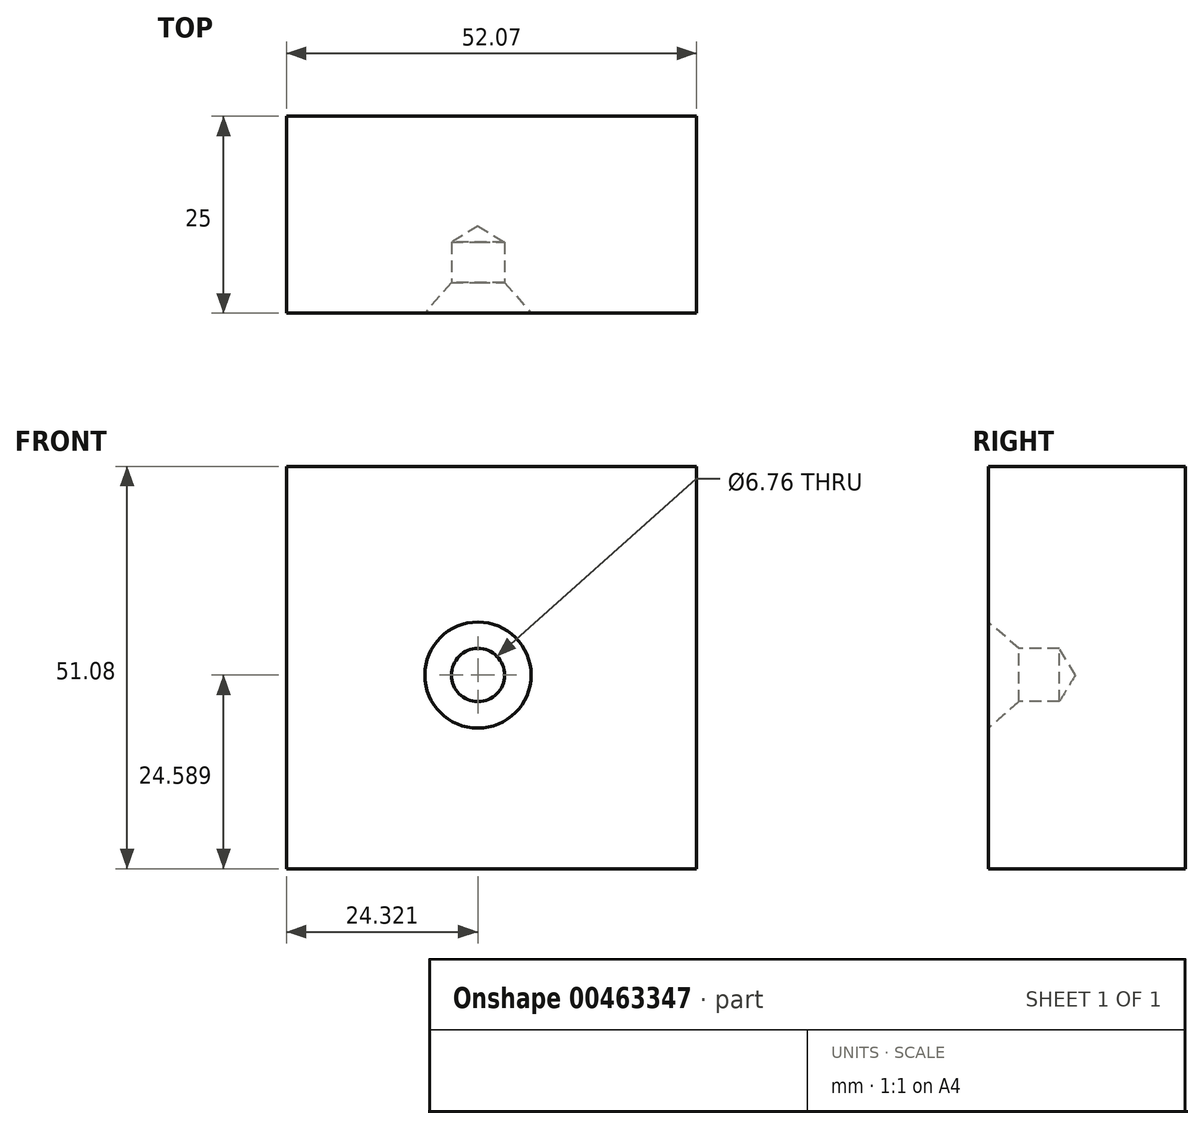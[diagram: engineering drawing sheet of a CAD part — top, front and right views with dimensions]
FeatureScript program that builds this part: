
annotation { "Feature Type Name" : "Feature", "Feature Type Description" : "" }
export const myFeature = defineFeature(function(context is Context, id is Id, definition is map)
    precondition{}
    {
        {
            var Q0;
            Q0=qCreatedBy(makeId("Front.planeOp"),FACE);
            var sketch = newSketch(context, id + "F0", { "sketchPlane" : qUnion([Q0])});
            skLineSegment(sketch, "E0.bottom", {"start": v(-102.8, 27.4) * mm, "end": v(-50.74, 27.4) * mm});
            skLineSegment(sketch, "E0.top", {"start": v(-102.8, 78.48) * mm, "end": v(-50.74, 78.48) * mm});
            skLineSegment(sketch, "E0.left", {"start": v(-102.8, 27.4) * mm, "end": v(-102.8, 78.48) * mm});
            skLineSegment(sketch, "E0.right", {"start": v(-50.74, 27.4) * mm, "end": v(-50.74, 78.48) * mm});
            skPoint(sketch, "E0.middle", {"position": v(-76.77, 52.94) * mm});
            skSolve(sketch);
        }
        {
            var Q0;
            Q0=makeQuery(id+"F0.imprint","IMPRINT",FACE,{"disambiguationData":[TD([[makeQuery(id+"F0.imprint","IMPRINT",EDGE,{"derivedFrom":sQuery(id+"F0.wireOp",EDGE,"E0.bottom")}),1.0]])]});
            extrude(context, id + "F1", {"entities" : qUnion([Q0]), "depth" : 25 * mm});
        }
        {
            var Q0;
            Q0=makeQuery(id+"F1.opExtrude","CAP_FACE",FACE,{"disambiguationData":[OSD([sQuery(id+"F0.wireOp",EDGE,"E0.bottom"),sQuery(id+"F0.wireOp",EDGE,"E0.top"),sQuery(id+"F0.wireOp",EDGE,"E0.left"),sQuery(id+"F0.wireOp",EDGE,"E0.right")])],"isStart":false});
            var sketch = newSketch(context, id + "F2", { "sketchPlane" : qUnion([Q0])});
            skPoint(sketch, "E1", {"position": v(-78.49, 51.99) * mm});
            skSolve(sketch);
        }
        {
            var Q0;
            Q0=sQuery(id+"F2.wireOp",VERTEX,"E1");
            var Q1;
            Q1=makeQuery(id+"F1.opExtrude","SWEPT_BODY",BODY,{"disambiguationData":[OSD([sQuery(id+"F0.wireOp",EDGE,"E0.bottom"),sQuery(id+"F0.wireOp",EDGE,"E0.top"),sQuery(id+"F0.wireOp",EDGE,"E0.left"),sQuery(id+"F0.wireOp",EDGE,"E0.right")])]});
            hole(context, id + "F3", {"style" : HoleStyle.C_SINK, "endStyle" : HoleEndStyle.BLIND, "standardTappedOrClearance" : lookupTablePath({ "standard" : "ANSI", "fit" : "Normal (ASME)", "size" : "1/4", "type" : "Clearance" }), "standardBlindInLast" : lookupTablePath({ "fit" : "Free", "standard" : "ANSI", "size" : "1/4", "type" : "Clearance" }), "holeDiameter" : 6.76 * mm, "cSinkDiameter" : 13.5 * mm, "cSinkAngle" : 82 * degree, "holeDepth" : 9 * mm, "isTappedThrough" : true, "tappedDepth" : 12 * mm, "tapClearance" : 3, "locations" : qUnion([Q0]), "scope" : qUnion([Q1])});
        }
    });
